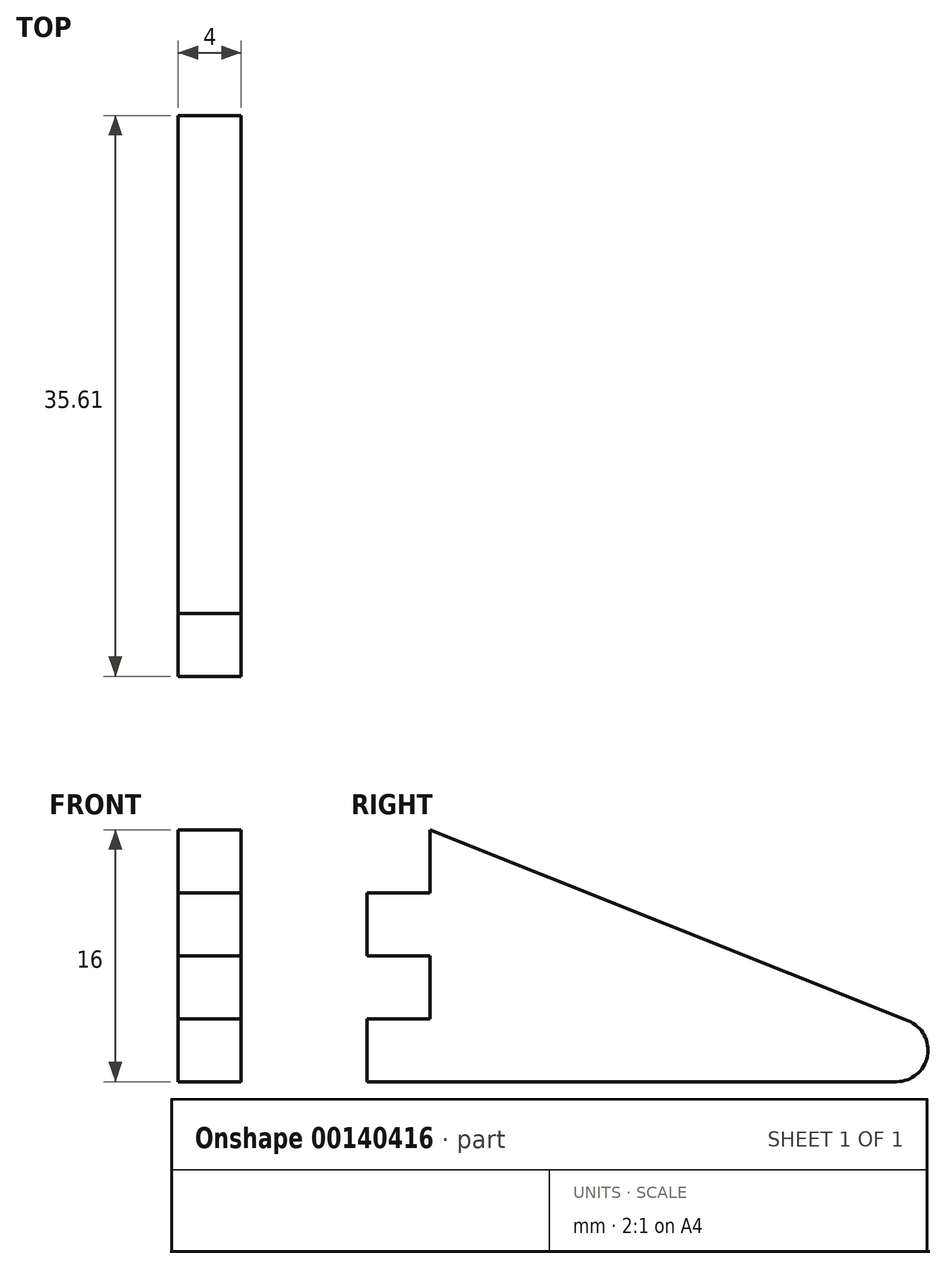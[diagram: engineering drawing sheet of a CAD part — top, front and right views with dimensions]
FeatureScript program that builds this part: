
annotation { "Feature Type Name" : "Feature", "Feature Type Description" : "" }
export const myFeature = defineFeature(function(context is Context, id is Id, definition is map)
    precondition{}
    {
        {
            var Q0;
            Q0=qCreatedBy(makeId("Right.planeOp"),FACE);
            var sketch = newSketch(context, id + "F0", { "sketchPlane" : qUnion([Q0])});
            skLineSegment(sketch, "E0.bottom", {"start": v(0, 0) * mm, "end": v(4, 0) * mm});
            skLineSegment(sketch, "E0.top", {"start": v(0, 4) * mm, "end": v(4, 4) * mm});
            skLineSegment(sketch, "E0.left", {"start": v(0, 0) * mm, "end": v(0, 4) * mm});
            skLineSegment(sketch, "E0.right", {"start": v(4, 0) * mm, "end": v(4, 4) * mm});
            skLineSegment(sketch, "E1", {"start": v(4, 4) * mm, "end": v(4, 8) * mm});
            skLineSegment(sketch, "E2.bottom", {"start": v(4, 8) * mm, "end": v(0, 8) * mm});
            skLineSegment(sketch, "E2.top", {"start": v(4, 12) * mm, "end": v(0, 12) * mm});
            skLineSegment(sketch, "E2.left", {"start": v(4, 8) * mm, "end": v(4, 12) * mm});
            skLineSegment(sketch, "E2.right", {"start": v(0, 8) * mm, "end": v(0, 12) * mm});
            skLineSegment(sketch, "E3", {"start": v(4, 12) * mm, "end": v(4, 16) * mm});
            skLineSegment(sketch, "E4", {"start": v(4, 16) * mm, "end": v(34.36, 3.86) * mm});
            skLineSegment(sketch, "E5", {"start": v(33.61, 0) * mm, "end": v(4, 0) * mm});
            skPoint(sketch, "E6.visualSharp", {"position": v(44, 0) * mm});
            skArc(sketch, "E6.filletArc", {"start": v(33.61, 0) * mm, "mid": v(35.58, 1.62) * mm, "end": v(34.36, 3.86) * mm});
            skSolve(sketch);
        }
        {
            var Q0;
            Q0=makeQuery(id+"F0.imprint","IMPRINT",FACE,{"disambiguationData":[TD([[makeQuery(id+"F0.imprint","IMPRINT",EDGE,{"derivedFrom":sQuery(id+"F0.wireOp",EDGE,"E0.right")}),-1.0]])]});
            var Q1;
            Q1=makeQuery(id+"F0.imprint","IMPRINT",FACE,{"disambiguationData":[TD([[makeQuery(id+"F0.imprint","IMPRINT",EDGE,{"derivedFrom":sQuery(id+"F0.wireOp",EDGE,"E2.bottom")}),-1.0]])]});
            var Q2;
            Q2=makeQuery(id+"F0.imprint","IMPRINT",FACE,{"disambiguationData":[TD([[makeQuery(id+"F0.imprint","IMPRINT",EDGE,{"derivedFrom":sQuery(id+"F0.wireOp",EDGE,"E0.bottom")}),1.0]])]});
            extrude(context, id + "F1", {"entities" : qUnion([Q0, Q1, Q2]), "depth" : 4 * mm});
        }
    });
